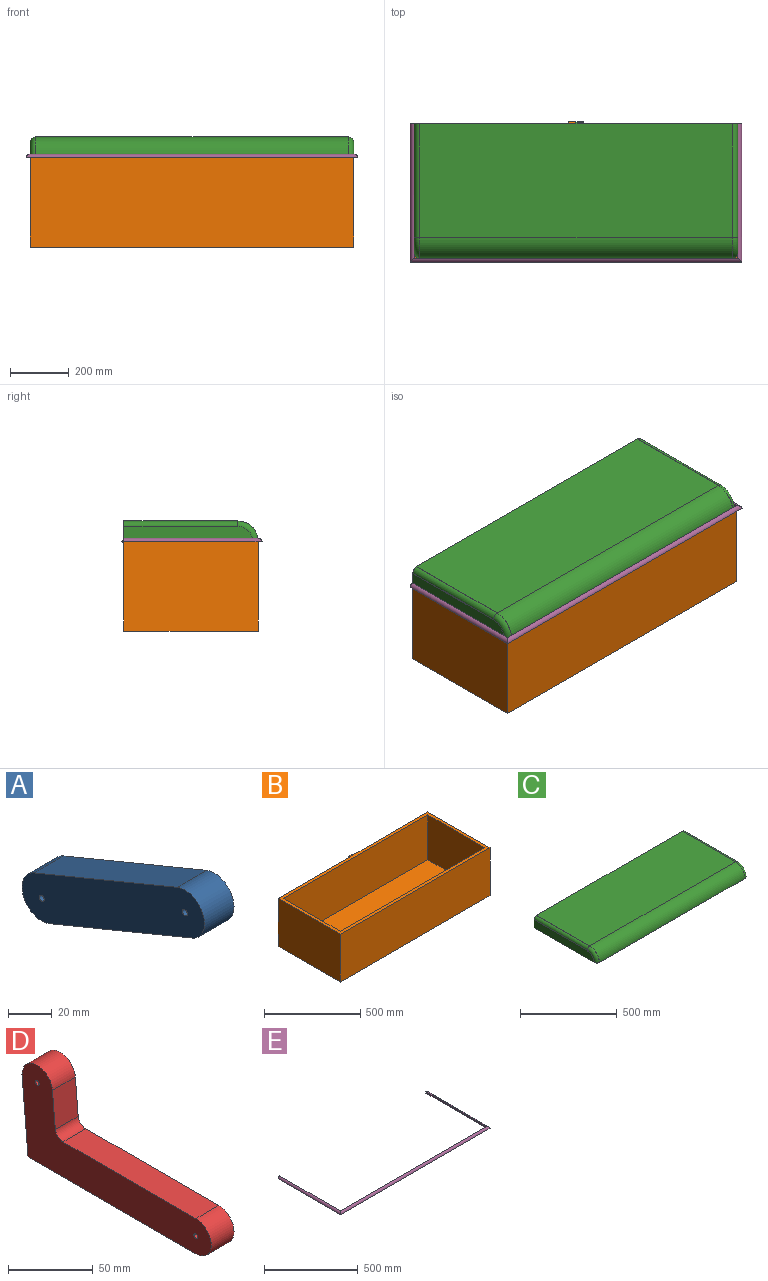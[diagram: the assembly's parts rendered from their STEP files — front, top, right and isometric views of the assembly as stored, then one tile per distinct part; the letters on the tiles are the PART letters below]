
ASSEMBLY  parts=5 mates=5
PART A: 8 faces, bbox 19.1x117.7x63.5 mm
  f0: plane 92.34x38.1mm, normal (0,0.38,0.92), area 1903mm2, adj f1,f4,f6,f7
  f1: cylinder r=12.7mm len=24.44mm, axis (1,0,0), area 760.1mm2, adj f0,f2,f6,f7
  f2: plane 92.34x38.1mm, normal (0,-0.38,-0.92), area 1903mm2, adj f1,f4,f6,f7
  f3: cylinder r=1.59mm len=19.05mm, axis (1,0,0), area 190mm2, adj f6,f7
  f4: cylinder r=12.7mm len=24.44mm, axis (1,0,0), area 760.1mm2, adj f0,f2,f6,f7
  f5: cylinder r=1.59mm len=19.05mm, axis (1,0,0), area 190mm2, adj f6,f7
  f6: plane 117.74x63.5mm, normal (-1,0,0), area 3028.2mm2, adj f0,f1,f2,f3,f4,f5
  f7: plane 117.74x63.5mm, normal (1,0,0), area 3028.2mm2, adj f0,f1,f2,f3,f4,f5
PART B: 15 faces, bbox 1101.7x463.6x308 mm
  f0: plane 1101.73x457.2mm, normal (0,0,1), area 57943.4mm2, adj f1,f2,f3,f4,f6,f7,f8,f9
  f1: plane 1101.73x304.8mm, normal (0,-1,0), area 335805.8mm2, adj f0,f2,f4,f5
  f2: plane 457.2x304.8mm, normal (1,0,0), area 139354.6mm2, adj f0,f1,f3,f5
  f3: plane 1101.73x304.8mm, normal (0,1,0), area 335725.1mm2, adj f0,f2,f4,f5,f12,f13,f14
  f4: plane 457.2x304.8mm, normal (-1,0,0), area 139354.6mm2, adj f0,f1,f3,f5
  f5: plane 1101.73x457.2mm, normal (0,0,-1), area 503708.7mm2, adj f1,f2,f3,f4
  f6: plane 1063.63x285.75mm, normal (0,1,0), area 303930.8mm2, adj f0,f7,f9,f10
  f7: plane 419.1x285.75mm, normal (-1,0,0), area 119757.8mm2, adj f0,f6,f8,f10
  f8: plane 1063.63x285.75mm, normal (0,-1,0), area 303930.8mm2, adj f0,f7,f9,f10
  f9: plane 419.1x285.75mm, normal (1,0,0), area 119757.8mm2, adj f0,f6,f8,f10
  f10: plane 1063.63x419.1mm, normal (0,0,1), area 445765.2mm2, adj f6,f7,f8,f9
  f11: cylinder r=3.17mm len=25.4mm, axis (1,0,0), area 380mm2, adj f0,f12,f13,f14
  f12: plane 25.4x3.18mm, normal (0,0,-1), area 80.6mm2, adj f3,f11,f13,f14
  f13: plane 6.35x6.35mm, normal (-1,0,0), area 33.8mm2, adj f3,f11,f12
  f14: plane 6.35x6.35mm, normal (1,0,0), area 33.8mm2, adj f3,f11,f12
PART C: 25 faces, bbox 1101.7x468.4x77.9 mm
  f0: plane 438.15x50.8mm, normal (1,0,0), area 21704.2mm2, adj f1,f5,f16,f19
  f1: plane 1101.73x69.85mm, normal (0,1,0), area 76672.6mm2, adj f0,f3,f4,f5,f11,f12,f13,f16
  f2: cylinder r=69.85mm len=1063.63mm, axis (1,0,0), area 116701.1mm2, adj f3,f5,f13,f17
  f3: plane 1063.63x387.35mm, normal (0,0,1), area 411995.1mm2, adj f1,f2,f13,f17
  f4: plane 438.15x50.8mm, normal (-1,0,0), area 21704.2mm2, adj f1,f5,f11,f14
  f5: plane 1101.73x457.2mm, normal (0,0,-1), area 57741.2mm2, adj f0,f1,f2,f4,f7,f8,f9,f10
  f6: plane 1063.63x368.3mm, normal (0,0,-1), area 391733.1mm2, adj f7,f8,f9,f10
  f7: plane 419.1x50.8mm, normal (-1,0,0), area 20736.5mm2, adj f5,f6,f8,f10
  f8: plane 1063.63x50.8mm, normal (0,-1,0), area 54032.2mm2, adj f5,f6,f7,f9
  f9: plane 419.1x50.8mm, normal (1,0,0), area 20736.5mm2, adj f5,f6,f8,f10
  f10: cylinder r=50.8mm len=1063.63mm, axis (1,0,0), area 84873.5mm2, adj f5,f6,f7,f9
  f11: plane 387.35x0.79mm, normal (0,0,1), area 307.5mm2, adj f1,f4,f12,f14
  f12: cylinder r=18.26mm len=387.35mm, axis (0,-1,0), area 11108mm2, adj f1,f11,f13,f15
  f13: plane 457.2x69.85mm, normal (-1,0,0), area 394.1mm2, adj f1,f2,f3,f5,f12,f15
  f14: cylinder r=50.8mm len=50.8mm, axis (1,0,0), area 63.3mm2, adj f4,f5,f11,f15
  f15: torus R=50.8mm, axis (1,0,0), area 2811.8mm2, adj f5,f12,f13,f14
  f16: plane 387.35x0.79mm, normal (0,0,1), area 307.5mm2, adj f0,f1,f18,f19
  f17: plane 457.2x69.85mm, normal (1,0,0), area 394.1mm2, adj f1,f2,f3,f5,f18,f20
  f18: cylinder r=18.26mm len=387.35mm, axis (0,-1,0), area 11108mm2, adj f1,f16,f17,f20
  f19: cylinder r=50.8mm len=50.8mm, axis (1,0,0), area 63.3mm2, adj f0,f5,f16,f20
  f20: torus R=50.8mm, axis (1,0,0), area 2811.8mm2, adj f5,f17,f18,f19
  f21: plane 25.4x3.18mm, normal (0,0,1), area 80.6mm2, adj f1,f22,f23,f24
  f22: cylinder r=3.17mm len=25.4mm, axis (-1,0,0), area 380mm2, adj f5,f21,f23,f24
  f23: plane 6.35x6.35mm, normal (1,0,0), area 33.8mm2, adj f1,f21,f22
  f24: plane 6.35x6.35mm, normal (-1,0,0), area 33.8mm2, adj f1,f21,f22
PART D: 11 faces, bbox 19.1x157.4x69.9 mm
  f0: cylinder r=12.7mm len=25.4mm, axis (-1,0,0), area 760.1mm2, adj f1,f6,f9,f10
  f1: plane 139.7x19.05mm, normal (0,0,-1), area 2661.3mm2, adj f0,f2,f9,f10
  f2: plane 57.15x19.05mm, normal (0,1,-0.09), area 1092.9mm2, adj f1,f3,f9,f10
  f3: cylinder r=12.7mm len=25.35mm, axis (-1,0,0), area 738.9mm2, adj f2,f4,f9,f10
  f4: plane 27.06x19.05mm, normal (0,-1,0.09), area 517.5mm2, adj f3,f5,f9,f10
  f5: cylinder r=6.35mm len=19.05mm, axis (-1,0,0), area 179.5mm2, adj f4,f6,f9,f10
  f6: plane 110.66x19.05mm, normal (0,0,1), area 2108mm2, adj f0,f5,f9,f10
  f7: cylinder r=1.59mm len=19.05mm, axis (-1,0,0), area 190mm2, adj f9,f10
  f8: cylinder r=1.59mm len=19.05mm, axis (-1,0,0), area 190mm2, adj f9,f10
  f9: plane 157.4x69.85mm, normal (1,0,0), area 4882.5mm2, adj f0,f1,f2,f3,f4,f5,f6,f7
  f10: plane 157.4x69.85mm, normal (-1,0,0), area 4882.5mm2, adj f0,f1,f2,f3,f4,f5,f6,f7
PART E: 13 faces, bbox 1127.1x469.9x12.7 mm
  f0: plane 12.7x12.7mm, normal (0,1,0), area 116.6mm2, adj f2,f3,f4,f9,f11
  f1: plane 12.7x12.7mm, normal (0,1,0), area 116.6mm2, adj f8,f9,f10,f11,f12
  f2: plane 457.2x11.11mm, normal (1,0,0), area 5080.6mm2, adj f0,f4,f7,f11
  f3: plane 463.55x1.59mm, normal (1,0,0), area 735.9mm2, adj f0,f6,f9,f11
  f4: cylinder r=12.7mm len=469.9mm, axis (0,1,0), area 9282mm2, adj f0,f2,f5,f9
  f5: cylinder r=12.7mm len=1127.13mm, axis (-1,0,0), area 22301mm2, adj f4,f7,f8,f9
  f6: plane 1114.43x1.59mm, normal (0,1,0), area 1769.1mm2, adj f3,f9,f10,f11
  f7: plane 1101.73x11.11mm, normal (0,1,0), area 12242.9mm2, adj f2,f5,f11,f12
  f8: cylinder r=12.7mm len=469.9mm, axis (0,-1,0), area 9282mm2, adj f1,f5,f9,f12
  f9: plane 1127.13x469.9mm, normal (0,0,-1), area 13044.3mm2, adj f0,f1,f3,f4,f5,f6,f8,f10
  f10: plane 463.55x1.59mm, normal (-1,0,0), area 735.9mm2, adj f1,f6,f9,f11
  f11: plane 1114.43x463.55mm, normal (0,0,-1), area 12883mm2, adj f0,f1,f2,f3,f6,f7,f10,f12
  f12: plane 457.2x11.11mm, normal (-1,0,0), area 5080.6mm2, adj f1,f7,f8,f11
PLACE A t=(531.81,0,0)mm
PLACE B at identity
PLACE C at identity
PLACE D t=(493.71,0,0)mm
PLACE E at identity
MATE revolute A.f3 <-> B.f7  axis (1,0,0) through (531.81,99.78,260.35)mm
MATE revolute A.f1 <-> D.f0  axis (-1,0,0) through (512.76,7.43,298.45)mm
MATE fastened C.f0 <-> E.f12  axis (1,0,0) through (550.86,228.6,304.8)mm
MATE cylindrical D.f3 <-> C.f7  axis (-1,0,0) through (512.76,139.43,342.9)mm
MATE revolute B.f11 <-> C.f22  axis (1,0,0) through (0,231.78,304.8)mm
